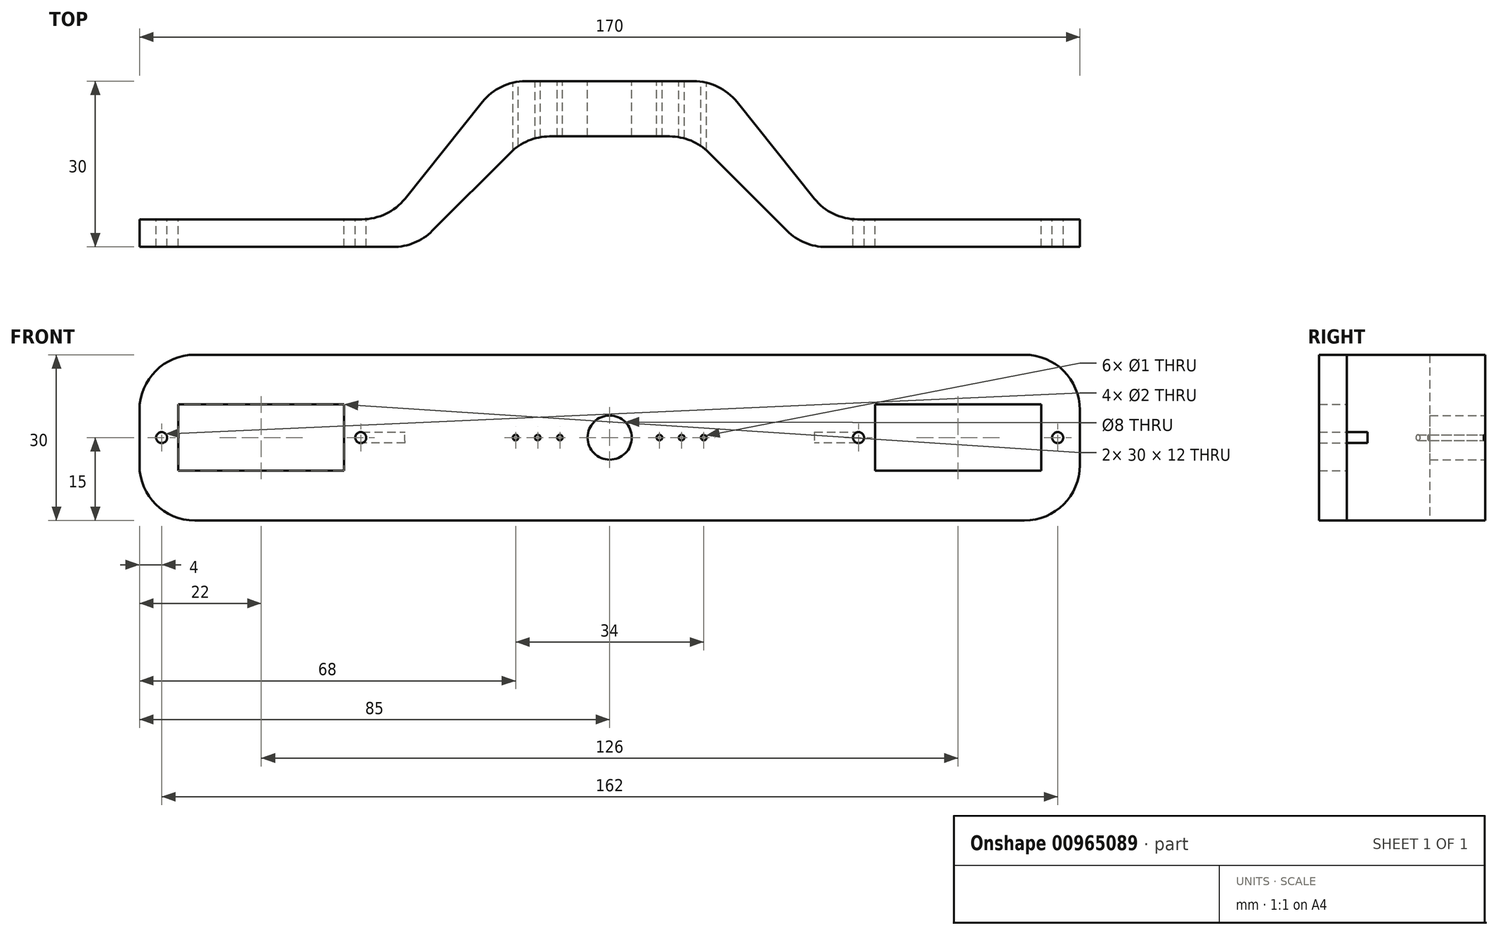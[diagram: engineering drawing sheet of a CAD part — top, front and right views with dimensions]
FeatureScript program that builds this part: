
annotation { "Feature Type Name" : "Feature", "Feature Type Description" : "" }
export const myFeature = defineFeature(function(context is Context, id is Id, definition is map)
    precondition{}
    {
        {
            var Q0;
            Q0=qCreatedBy(makeId("Top.planeOp"),FACE);
            var sketch = newSketch(context, id + "F0", { "sketchPlane" : qUnion([Q0])});
            skLineSegment(sketch, "E0", {"start": v(20, 30) * mm, "end": v(-20, 30) * mm});
            skLineSegment(sketch, "E1", {"start": v(-20, 30) * mm, "end": v(-40, 5) * mm});
            skLineSegment(sketch, "E2", {"start": v(-40, 5) * mm, "end": v(-85, 5) * mm});
            skLineSegment(sketch, "E3", {"start": v(-85, 5) * mm, "end": v(-85, 0) * mm});
            skLineSegment(sketch, "E4", {"start": v(85, 0) * mm, "end": v(85, 5) * mm});
            skLineSegment(sketch, "E5", {"start": v(85, 5) * mm, "end": v(40, 5) * mm});
            skLineSegment(sketch, "E6", {"start": v(40, 5) * mm, "end": v(20, 30) * mm});
            skLineSegment(sketch, "E7", {"start": v(-85, 0) * mm, "end": v(-35, 0) * mm});
            skLineSegment(sketch, "E8", {"start": v(-35, 0) * mm, "end": v(-15, 20) * mm});
            skLineSegment(sketch, "E9", {"start": v(-15, 20) * mm, "end": v(15, 20) * mm});
            skLineSegment(sketch, "E10", {"start": v(15, 20) * mm, "end": v(35, 0) * mm});
            skLineSegment(sketch, "E11", {"start": v(35, 0) * mm, "end": v(85, 0) * mm});
            skSolve(sketch);
        }
        {
            var Q0;
            Q0=makeQuery(id+"F0.imprint","IMPRINT",FACE,{"disambiguationData":[TD([[makeQuery(id+"F0.imprint","IMPRINT",EDGE,{"derivedFrom":sQuery(id+"F0.wireOp",EDGE,"E0")}),1.0]])]});
            extrude(context, id + "F1", {"entities" : qUnion([Q0]), "depth" : 30 * mm, "offsetDistance" : 25 * mm});
        }
        {
            var Q0;
            Q0=makeQuery(id+"F1.opExtrude","SWEPT_FACE",FACE,{"disambiguationData":[OSD([sQuery(id+"F0.wireOp",EDGE,"E5")])]});
            var sketch = newSketch(context, id + "F2", { "sketchPlane" : qUnion([Q0])});
            skLineSegment(sketch, "E12.bottom", {"start": v(78, 9) * mm, "end": v(48, 9) * mm});
            skLineSegment(sketch, "E12.top", {"start": v(78, 21) * mm, "end": v(48, 21) * mm});
            skLineSegment(sketch, "E12.left", {"start": v(78, 9) * mm, "end": v(78, 21) * mm});
            skLineSegment(sketch, "E12.right", {"start": v(48, 9) * mm, "end": v(48, 21) * mm});
            skLineSegment(sketch, "E13.bottom", {"start": v(-48, 9) * mm, "end": v(-78, 9) * mm});
            skLineSegment(sketch, "E13.top", {"start": v(-48, 21) * mm, "end": v(-78, 21) * mm});
            skLineSegment(sketch, "E13.left", {"start": v(-48, 9) * mm, "end": v(-48, 21) * mm});
            skLineSegment(sketch, "E13.right", {"start": v(-78, 9) * mm, "end": v(-78, 21) * mm});
            skCircle(sketch, "E14", {"center": v(81, 15) * mm, "radius": 1 * mm});
            skCircle(sketch, "E15", {"center": v(45, 15) * mm, "radius": 1 * mm});
            skCircle(sketch, "E16", {"center": v(-81, 15) * mm, "radius": 1 * mm});
            skCircle(sketch, "E17", {"center": v(-45, 15) * mm, "radius": 1 * mm});
            skSolve(sketch);
        }
        {
            var Q0;
            Q0=makeQuery(id+"F2.imprint","IMPRINT",FACE,{"disambiguationData":[TD([[makeQuery(id+"F2.imprint","IMPRINT",EDGE,{"derivedFrom":sQuery(id+"F2.wireOp",EDGE,"E12.bottom")}),-1.0]])]});
            var Q1;
            Q1=makeQuery(id+"F2.imprint","IMPRINT",FACE,{"disambiguationData":[TD([[makeQuery(id+"F2.imprint","IMPRINT",EDGE,{"derivedFrom":sQuery(id+"F2.wireOp",EDGE,"E13.bottom")}),-1.0]])]});
            var Q2;
            Q2=makeQuery(id+"F2.imprint","IMPRINT",FACE,{"disambiguationData":[TD([[makeQuery(id+"F2.imprint","IMPRINT",EDGE,{"derivedFrom":sQuery(id+"F2.wireOp",EDGE,"E17")}),1.0]])]});
            var Q3;
            Q3=makeQuery(id+"F2.imprint","IMPRINT",FACE,{"disambiguationData":[TD([[makeQuery(id+"F2.imprint","IMPRINT",EDGE,{"derivedFrom":sQuery(id+"F2.wireOp",EDGE,"E16")}),1.0]])]});
            var Q4;
            Q4=makeQuery(id+"F2.imprint","IMPRINT",FACE,{"disambiguationData":[TD([[makeQuery(id+"F2.imprint","IMPRINT",EDGE,{"derivedFrom":sQuery(id+"F2.wireOp",EDGE,"E15")}),1.0]])]});
            var Q5;
            Q5=makeQuery(id+"F2.imprint","IMPRINT",FACE,{"disambiguationData":[TD([[makeQuery(id+"F2.imprint","IMPRINT",EDGE,{"derivedFrom":sQuery(id+"F2.wireOp",EDGE,"E14")}),1.0]])]});
            extrude(context, id + "F3", {"entities" : qUnion([Q0, Q1, Q2, Q3, Q4, Q5]), "operationType" : NewBodyOperationType.REMOVE, "oppositeDirection" : true, "depth" : 25 * mm, "offsetDistance" : 25 * mm});
        }
        {
            var Q0;
            Q0=makeQuery(id+"F1.opExtrude","SWEPT_FACE",FACE,{"disambiguationData":[OSD([sQuery(id+"F0.wireOp",EDGE,"E0")])]});
            var sketch = newSketch(context, id + "F4", { "sketchPlane" : qUnion([Q0])});
            skCircle(sketch, "E18", {"center": v(0, 15) * mm, "radius": 4 * mm});
            skCircle(sketch, "E19", {"center": v(-9, 15) * mm, "radius": 0.5 * mm});
            skCircle(sketch, "E20", {"center": v(9, 15) * mm, "radius": 0.5 * mm});
            skCircle(sketch, "E21", {"center": v(-13, 15) * mm, "radius": 0.5 * mm});
            skCircle(sketch, "E22", {"center": v(-17, 15) * mm, "radius": 0.5 * mm});
            skCircle(sketch, "E23", {"center": v(13, 15) * mm, "radius": 0.5 * mm});
            skCircle(sketch, "E24", {"center": v(17, 15) * mm, "radius": 0.5 * mm});
            skSolve(sketch);
        }
        {
            var Q0;
            Q0=makeQuery(id+"F4.imprint","IMPRINT",FACE,{"disambiguationData":[TD([[makeQuery(id+"F4.imprint","IMPRINT",EDGE,{"derivedFrom":sQuery(id+"F4.wireOp",EDGE,"E18")}),1.0]])]});
            var Q1;
            Q1=makeQuery(id+"F4.imprint","IMPRINT",FACE,{"disambiguationData":[TD([[makeQuery(id+"F4.imprint","IMPRINT",EDGE,{"derivedFrom":sQuery(id+"F4.wireOp",EDGE,"E20")}),1.0]])]});
            var Q2;
            Q2=makeQuery(id+"F4.imprint","IMPRINT",FACE,{"disambiguationData":[TD([[makeQuery(id+"F4.imprint","IMPRINT",EDGE,{"derivedFrom":sQuery(id+"F4.wireOp",EDGE,"E23")}),1.0]])]});
            var Q3;
            Q3=makeQuery(id+"F4.imprint","IMPRINT",FACE,{"disambiguationData":[TD([[makeQuery(id+"F4.imprint","IMPRINT",EDGE,{"derivedFrom":sQuery(id+"F4.wireOp",EDGE,"E24")}),1.0]])]});
            var Q4;
            Q4=makeQuery(id+"F4.imprint","IMPRINT",FACE,{"disambiguationData":[TD([[makeQuery(id+"F4.imprint","IMPRINT",EDGE,{"derivedFrom":sQuery(id+"F4.wireOp",EDGE,"E19")}),1.0]])]});
            var Q5;
            Q5=makeQuery(id+"F4.imprint","IMPRINT",FACE,{"disambiguationData":[TD([[makeQuery(id+"F4.imprint","IMPRINT",EDGE,{"derivedFrom":sQuery(id+"F4.wireOp",EDGE,"E21")}),1.0]])]});
            var Q6;
            Q6=makeQuery(id+"F4.imprint","IMPRINT",FACE,{"disambiguationData":[TD([[makeQuery(id+"F4.imprint","IMPRINT",EDGE,{"derivedFrom":sQuery(id+"F4.wireOp",EDGE,"E22")}),1.0]])]});
            extrude(context, id + "F5", {"entities" : qUnion([Q0, Q1, Q2, Q3, Q4, Q5, Q6]), "operationType" : NewBodyOperationType.REMOVE, "oppositeDirection" : true, "depth" : 25 * mm, "offsetDistance" : 25 * mm});
        }
        {
            var Q0;
            Q0=makeQuery(id+"F1.opExtrude","CAP_EDGE",EDGE,{"disambiguationData":[OSD([sQuery(id+"F0.wireOp",EDGE,"E3")])],"isStart":false});
            var Q1;
            Q1=makeQuery(id+"F1.opExtrude","CAP_EDGE",EDGE,{"disambiguationData":[OSD([sQuery(id+"F0.wireOp",EDGE,"E3")])],"isStart":true});
            var Q2;
            Q2=makeQuery(id+"F1.opExtrude","CAP_EDGE",EDGE,{"disambiguationData":[OSD([sQuery(id+"F0.wireOp",EDGE,"E4")])],"isStart":false});
            var Q3;
            Q3=makeQuery(id+"F1.opExtrude","CAP_EDGE",EDGE,{"disambiguationData":[OSD([sQuery(id+"F0.wireOp",EDGE,"E4")])],"isStart":true});
            var Q4;
            Q4=makeQuery(id+"F1.opExtrude","SWEPT_EDGE",EDGE,{"disambiguationData":[OSD([sQuery(id+"F0.wireOp",EDGE,"E5"),sQuery(id+"F0.wireOp",EDGE,"E6")])]});
            var Q5;
            Q5=makeQuery(id+"F1.opExtrude","SWEPT_EDGE",EDGE,{"disambiguationData":[OSD([sQuery(id+"F0.wireOp",EDGE,"E1"),sQuery(id+"F0.wireOp",EDGE,"E2")])]});
            var Q6;
            Q6=makeQuery(id+"F1.opExtrude","SWEPT_EDGE",EDGE,{"disambiguationData":[OSD([sQuery(id+"F0.wireOp",EDGE,"E0"),sQuery(id+"F0.wireOp",EDGE,"E1")])]});
            var Q7;
            Q7=makeQuery(id+"F1.opExtrude","SWEPT_EDGE",EDGE,{"disambiguationData":[OSD([sQuery(id+"F0.wireOp",EDGE,"E0"),sQuery(id+"F0.wireOp",EDGE,"E6")])]});
            var Q8;
            Q8=makeQuery(id+"F1.opExtrude","SWEPT_EDGE",EDGE,{"disambiguationData":[OSD([sQuery(id+"F0.wireOp",EDGE,"E7"),sQuery(id+"F0.wireOp",EDGE,"E8")])]});
            var Q9;
            Q9=makeQuery(id+"F1.opExtrude","SWEPT_EDGE",EDGE,{"disambiguationData":[OSD([sQuery(id+"F0.wireOp",EDGE,"E8"),sQuery(id+"F0.wireOp",EDGE,"E9")])]});
            var Q10;
            Q10=makeQuery(id+"F1.opExtrude","SWEPT_EDGE",EDGE,{"disambiguationData":[OSD([sQuery(id+"F0.wireOp",EDGE,"E9"),sQuery(id+"F0.wireOp",EDGE,"E10")])]});
            var Q11;
            Q11=makeQuery(id+"F1.opExtrude","SWEPT_EDGE",EDGE,{"disambiguationData":[OSD([sQuery(id+"F0.wireOp",EDGE,"E10"),sQuery(id+"F0.wireOp",EDGE,"E11")])]});
            fillet(context, id + "F6", {"entities" : qUnion([Q0, Q1, Q2, Q3, Q4, Q5, Q6, Q7, Q8, Q9, Q10, Q11]), "radius" : 10 * mm, "tangentPropagation" : true, "allowEdgeOverflow" : false});
        }
    });
